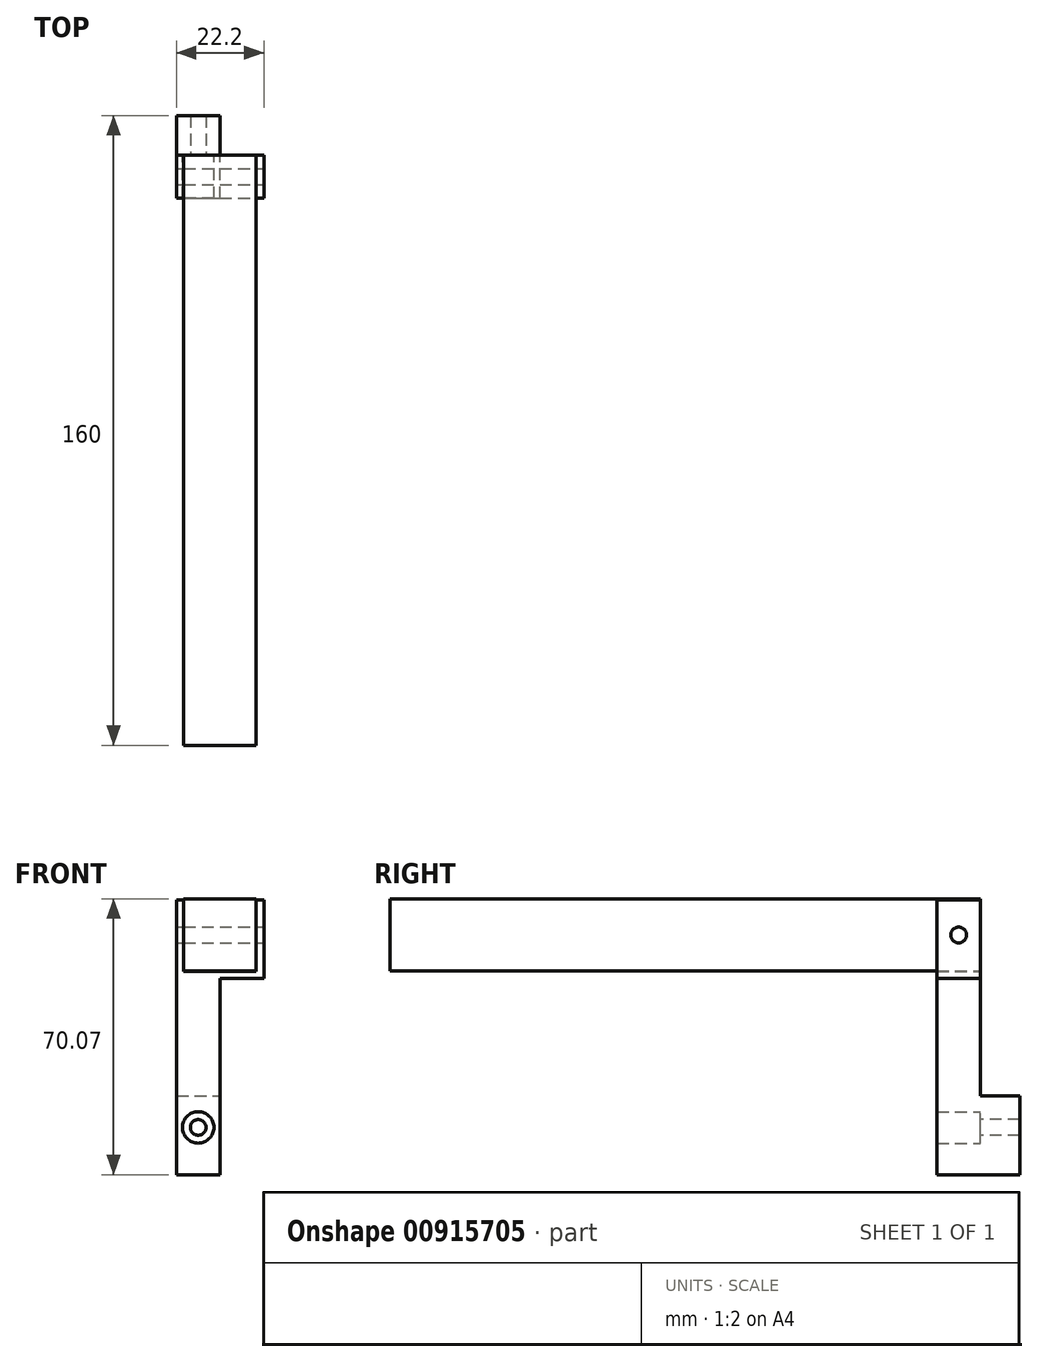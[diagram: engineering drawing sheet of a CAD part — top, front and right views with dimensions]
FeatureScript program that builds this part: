
annotation { "Feature Type Name" : "Feature", "Feature Type Description" : "" }
export const myFeature = defineFeature(function(context is Context, id is Id, definition is map)
    precondition{}
    {
        {
            var Q0;
            Q0=qCreatedBy(makeId("Front.planeOp"),FACE);
            var sketch = newSketch(context, id + "F0", { "sketchPlane" : qUnion([Q0])});
            skLineSegment(sketch, "E0.bottom", {"start": v(-9.17, 9.18) * mm, "end": v(9.18, 9.18) * mm});
            skLineSegment(sketch, "E0.top", {"start": v(-9.18, -9.18) * mm, "end": v(9.17, -9.18) * mm});
            skLineSegment(sketch, "E0.left", {"start": v(-9.17, 9.18) * mm, "end": v(-9.18, -9.17) * mm});
            skLineSegment(sketch, "E0.right", {"start": v(9.18, 9.18) * mm, "end": v(9.18, -9.17) * mm});
            skPoint(sketch, "E0.middle", {"position": v(0, 0) * mm});
            skSolve(sketch);
        }
        {
            var Q0;
            Q0=makeQuery(id+"F0.imprint","IMPRINT",FACE,{"disambiguationData":[TD([[makeQuery(id+"F0.imprint","IMPRINT",EDGE,{"derivedFrom":sQuery(id+"F0.wireOp",EDGE,"E0.bottom")}),-1.0]])]});
            extrude(context, id + "F1", {"entities" : qUnion([Q0]), "depth" : 150 * mm, "offsetDistance" : 25 * mm});
        }
        {
            var Q0;
            Q0=qCreatedBy(makeId("Front.planeOp"),FACE);
            var sketch = newSketch(context, id + "F2", { "sketchPlane" : qUnion([Q0])});
            skLineSegment(sketch, "E1", {"start": v(-11, 8.97) * mm, "end": v(-11, -60.89) * mm});
            skLineSegment(sketch, "E2", {"start": v(-11, -60.89) * mm, "end": v(0, -60.89) * mm});
            skLineSegment(sketch, "E3", {"start": v(0, -60.89) * mm, "end": v(0, -11.03) * mm});
            skLineSegment(sketch, "E4", {"start": v(0, -11.03) * mm, "end": v(11.2, -11.03) * mm});
            skLineSegment(sketch, "E5", {"start": v(11.2, -11.03) * mm, "end": v(11.2, 8.97) * mm});
            skLineSegment(sketch, "E6", {"start": v(-11, 8.97) * mm, "end": v(-9.18, 8.97) * mm});
            skLineSegment(sketch, "E7", {"start": v(-9.18, 8.97) * mm, "end": v(-9.18, -9.19) * mm});
            skLineSegment(sketch, "E8", {"start": v(-9.18, -9.19) * mm, "end": v(9.18, -9.19) * mm});
            skLineSegment(sketch, "E9", {"start": v(9.18, -9.19) * mm, "end": v(9.18, 8.97) * mm});
            skLineSegment(sketch, "E10", {"start": v(11.2, 8.97) * mm, "end": v(9.18, 8.97) * mm});
            skSolve(sketch);
        }
        {
            var Q0;
            Q0=makeQuery(id+"F2.imprint","IMPRINT",FACE,{"disambiguationData":[TD([[makeQuery(id+"F2.imprint","IMPRINT",EDGE,{"derivedFrom":sQuery(id+"F2.wireOp",EDGE,"E1")}),1.0]])]});
            extrude(context, id + "F3", {"entities" : qUnion([Q0]), "depth" : (11) * mm, "offsetDistance" : 25 * mm});
        }
        {
            var Q0;
            Q0=makeQuery(id+"F3.opExtrude","SWEPT_FACE",FACE,{"disambiguationData":[OSD([sQuery(id+"F2.wireOp",EDGE,"E5")])]});
            var sketch = newSketch(context, id + "F4", { "sketchPlane" : qUnion([Q0])});
            skLineSegment(sketch, "E11", {"start": v(-11, 0) * mm, "end": v(0, 0) * mm, "construction": true});
            skLineSegment(sketch, "E12", {"start": v(-5.5, 8.97) * mm, "end": v(-5.5, -40.78) * mm, "construction": true});
            skLineSegment(sketch, "E13", {"start": v(-9.2, -41.08) * mm, "end": v(-9.2, -31.08) * mm, "construction": true});
            skCircle(sketch, "E14", {"center": v(-5.5, 0) * mm, "radius": 2 * mm});
            skCircle(sketch, "E15", {"center": v(-5.5, -31.08) * mm, "radius": 1.7 * mm});
            skSolve(sketch);
        }
        {
            var Q0;
            Q0=makeQuery(id+"F4.imprint","IMPRINT",FACE,{"disambiguationData":[TD([[makeQuery(id+"F4.imprint","IMPRINT",EDGE,{"derivedFrom":sQuery(id+"F4.wireOp",EDGE,"E14")}),1.0]])]});
            extrude(context, id + "F5", {"entities" : qUnion([Q0]), "operationType" : NewBodyOperationType.REMOVE, "oppositeDirection" : true, "depth" : 25 * mm, "offsetDistance" : 25 * mm});
        }
        {
            var Q0;
            Q0=qCreatedBy(makeId("Right.planeOp"),FACE);
            var sketch = newSketch(context, id + "F6", { "sketchPlane" : qUnion([Q0])});
            skLineSegment(sketch, "E16", {"start": v(0, -60.88) * mm, "end": v(0, -40.88) * mm, "construction": true});
            skLineSegment(sketch, "E17", {"start": v(0, -40.88) * mm, "end": v(10, -40.88) * mm});
            skLineSegment(sketch, "E18", {"start": v(10, -40.88) * mm, "end": v(10, -60.88) * mm});
            skLineSegment(sketch, "E19", {"start": v(10, -60.88) * mm, "end": v(0, -60.88) * mm});
            skLineSegment(sketch, "E20", {"start": v(0, -60.88) * mm, "end": v(0, -40.88) * mm});
            skSolve(sketch);
        }
        {
            var Q0;
            Q0=makeQuery(id+"F6.imprint","IMPRINT",FACE,{"disambiguationData":[TD([[makeQuery(id+"F6.imprint","IMPRINT",EDGE,{"derivedFrom":sQuery(id+"F6.wireOp",EDGE,"E17")}),-1.0]])]});
            var Q1;
            Q1=makeQuery(id+"F3.opExtrude","SWEPT_FACE",FACE,{"disambiguationData":[OSD([sQuery(id+"F2.wireOp",EDGE,"E1")])]});
            extrude(context, id + "F7", {"entities" : qUnion([Q0]), "operationType" : NewBodyOperationType.ADD, "endBound" : BoundingType.UP_TO_SURFACE, "oppositeDirection" : true, "depth" : 25 * mm, "endBoundEntityFace" : qUnion([Q1]), "offsetDistance" : 25 * mm});
        }
        {
            var Q0;
            Q0=qCreatedBy(makeId("Front.planeOp"),FACE);
            var sketch = newSketch(context, id + "F8", { "sketchPlane" : qUnion([Q0])});
            skCircle(sketch, "E21", {"center": v(-5.5, -48.88) * mm, "radius": 2 * mm});
            skCircle(sketch, "E22", {"center": v(-5.5, -48.88) * mm, "radius": 4 * mm});
            skSolve(sketch);
        }
        {
            var Q0;
            Q0=makeQuery(id+"F8.imprint","IMPRINT",FACE,{"disambiguationData":[TD([[makeQuery(id+"F8.imprint","IMPRINT",EDGE,{"derivedFrom":sQuery(id+"F8.wireOp",EDGE,"E21")}),1.0]])]});
            extrude(context, id + "F9", {"entities" : qUnion([Q0]), "operationType" : NewBodyOperationType.REMOVE, "endBound" : BoundingType.SYMMETRIC, "oppositeDirection" : true, "depth" : 25 * mm, "offsetDistance" : 25 * mm});
        }
        {
            var Q0;
            Q0=makeQuery(id+"F8.imprint","IMPRINT",FACE,{"disambiguationData":[TD([[makeQuery(id+"F8.imprint","IMPRINT",EDGE,{"derivedFrom":sQuery(id+"F8.wireOp",EDGE,"E21")}),-1.0]])]});
            var Q1;
            Q1=makeQuery(id+"F3.opExtrude","CAP_FACE",FACE,{"disambiguationData":[OSD([sQuery(id+"F2.wireOp",EDGE,"E1"),sQuery(id+"F2.wireOp",EDGE,"E2"),sQuery(id+"F2.wireOp",EDGE,"E3"),sQuery(id+"F2.wireOp",EDGE,"E4"),sQuery(id+"F2.wireOp",EDGE,"E5"),sQuery(id+"F2.wireOp",EDGE,"E6"),sQuery(id+"F2.wireOp",EDGE,"E7"),sQuery(id+"F2.wireOp",EDGE,"E8"),sQuery(id+"F2.wireOp",EDGE,"E9"),sQuery(id+"F2.wireOp",EDGE,"E10")])],"isStart":false});
            extrude(context, id + "F10", {"entities" : qUnion([Q0]), "operationType" : NewBodyOperationType.REMOVE, "endBound" : BoundingType.UP_TO_SURFACE, "depth" : 11.1 * mm, "endBoundEntityFace" : qUnion([Q1]), "offsetDistance" : 25 * mm});
        }
    });
